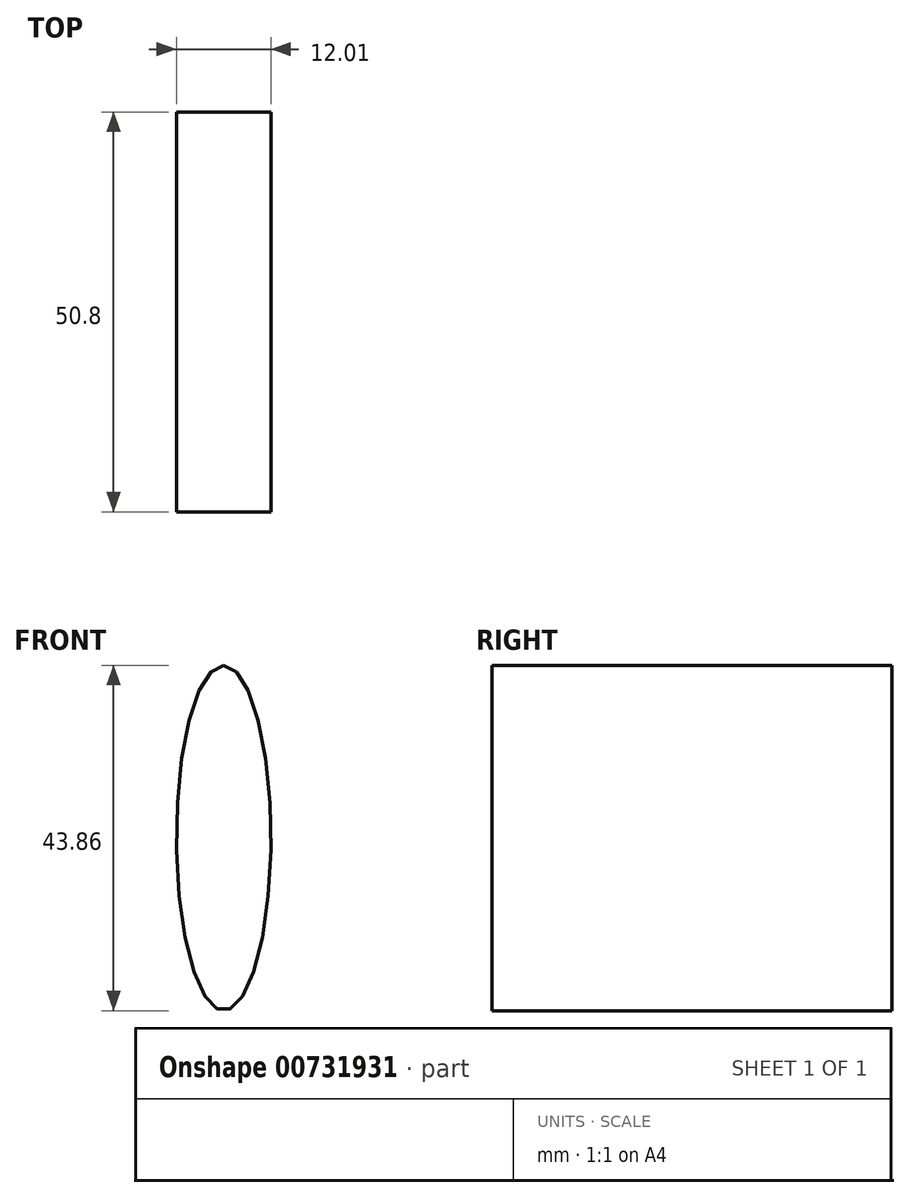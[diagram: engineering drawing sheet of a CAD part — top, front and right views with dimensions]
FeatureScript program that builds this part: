
annotation { "Feature Type Name" : "Feature", "Feature Type Description" : "" }
export const myFeature = defineFeature(function(context is Context, id is Id, definition is map)
    precondition{}
    {
        {
            var Q0;
            Q0=qCreatedBy(makeId("Front.planeOp"),FACE);
            var sketch = newSketch(context, id + "F0", { "sketchPlane" : qUnion([Q0])});
            skEllipse(sketch, "E0", {"center": v(26.66, 24.7) * mm, "majorRadius": 21 * mm, "minorRadius": 1.33 * mm, "majorAxis": v(1, 0)});
            skEllipse(sketch, "E1", {"center": v(-15.57, 0) * mm, "majorRadius": 21.93 * mm, "minorRadius": 6 * mm, "majorAxis": v(0, 1)});
            skSolve(sketch);
        }
        {
            var Q0;
            Q0=makeQuery(id+"F0.imprint","IMPRINT",FACE,{"disambiguationData":[TD([[makeQuery(id+"F0.imprint","IMPRINT",EDGE,{"derivedFrom":sQuery(id+"F0.wireOp",EDGE,"E1")}),1.0]])]});
            extrude(context, id + "F1", {"entities" : qUnion([Q0]), "depth" : 50.8 * mm, "offsetDistance" : 25.4 * mm});
        }
    });
